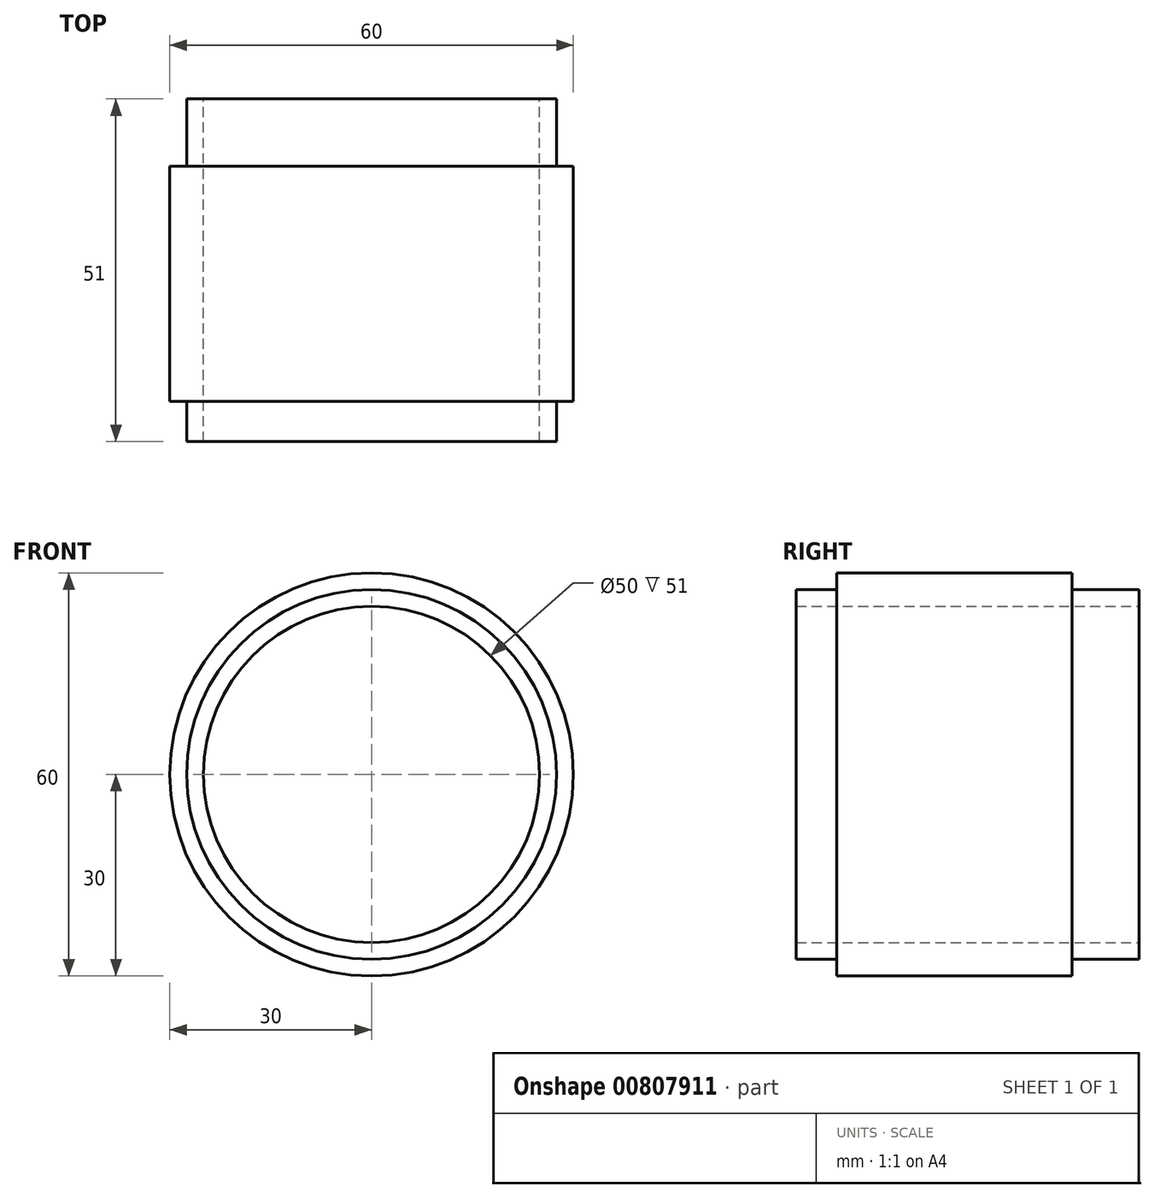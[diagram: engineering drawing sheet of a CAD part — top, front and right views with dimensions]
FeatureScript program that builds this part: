
annotation { "Feature Type Name" : "Feature", "Feature Type Description" : "" }
export const myFeature = defineFeature(function(context is Context, id is Id, definition is map)
    precondition{}
    {
        {
            var Q0;
            Q0=qCreatedBy(makeId("Front.planeOp"),FACE);
            var sketch = newSketch(context, id + "F0", { "sketchPlane" : qUnion([Q0])});
            skCircle(sketch, "E0", {"center": v(0, 0) * mm, "radius": 30 * mm});
            skCircle(sketch, "E1", {"center": v(0, 0) * mm, "radius": 27.5 * mm});
            skCircle(sketch, "E2", {"center": v(0, 0) * mm, "radius": 25 * mm});
            skSolve(sketch);
        }
        {
            var Q0;
            Q0=makeQuery(id+"F0.imprint","IMPRINT",FACE,{"disambiguationData":[TD([[makeQuery(id+"F0.imprint","IMPRINT",EDGE,{"derivedFrom":sQuery(id+"F0.wireOp",EDGE,"E1")}),1.0]])]});
            var Q1;
            Q1=makeQuery(id+"F0.imprint","IMPRINT",FACE,{"disambiguationData":[TD([[makeQuery(id+"F0.imprint","IMPRINT",EDGE,{"derivedFrom":sQuery(id+"F0.wireOp",EDGE,"E0")}),1.0]])]});
            extrude(context, id + "F1", {"entities" : qUnion([Q0, Q1]), "depth" : 35 * mm, "offsetDistance" : 25 * mm});
        }
        {
            var Q0;
            Q0=makeQuery(id+"F0.imprint","IMPRINT",FACE,{"disambiguationData":[TD([[makeQuery(id+"F0.imprint","IMPRINT",EDGE,{"derivedFrom":sQuery(id+"F0.wireOp",EDGE,"E1")}),1.0]])]});
            extrude(context, id + "F2", {"entities" : qUnion([Q0]), "operationType" : NewBodyOperationType.ADD, "oppositeDirection" : true, "depth" : 10 * mm, "offsetDistance" : 25 * mm});
        }
        {
            var Q0;
            Q0=makeQuery(id+"F1.opExtrude","CAP_FACE",FACE,{"disambiguationData":[OSD([sQuery(id+"F0.wireOp",EDGE,"E0"),sQuery(id+"F0.wireOp",EDGE,"E2")])],"isStart":false});
            var sketch = newSketch(context, id + "F3", { "sketchPlane" : qUnion([Q0])});
            skCircle(sketch, "E3", {"center": v(0, 0) * mm, "radius": 27.5 * mm});
            skSolve(sketch);
        }
        {
            var Q0;
            Q0=makeQuery(id+"F3.imprint","IMPRINT",FACE,{"disambiguationData":[TD([[makeQuery(id+"F3.imprint","IMPRINT",EDGE,{"derivedFrom":sQuery(id+"F3.wireOp",EDGE,"E3")}),1.0]])]});
            extrude(context, id + "F4", {"entities" : qUnion([Q0]), "operationType" : NewBodyOperationType.ADD, "depth" : 6 * mm, "offsetDistance" : 25 * mm});
        }
    });
